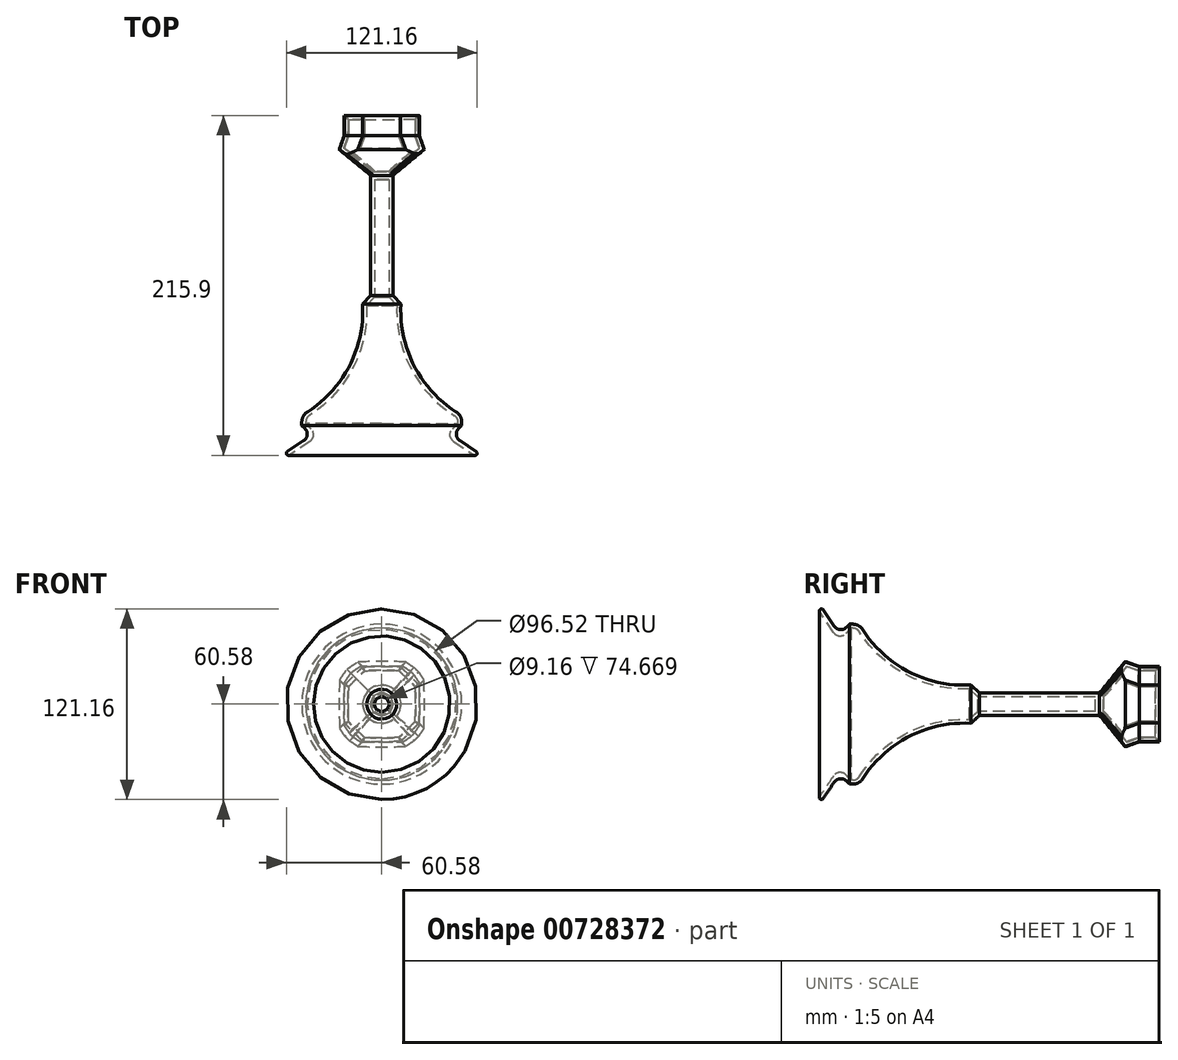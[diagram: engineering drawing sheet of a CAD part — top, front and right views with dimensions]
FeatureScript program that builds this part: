
annotation { "Feature Type Name" : "Feature", "Feature Type Description" : "" }
export const myFeature = defineFeature(function(context is Context, id is Id, definition is map)
    precondition{}
    {
        {
            var Q0;
            Q0=qCreatedBy(makeId("Top.planeOp"),FACE);
            var sketch = newSketch(context, id + "F0", { "sketchPlane" : qUnion([Q0])});
            skLineSegment(sketch, "E0", {"start": v(0, 0) * mm, "end": v(-50.8, 0) * mm});
            skLineSegment(sketch, "E1", {"start": v(0, 0) * mm, "end": v(50.8, 0) * mm});
            skLineSegment(sketch, "E2", {"start": v(-50.8, 0) * mm, "end": v(-50.8, 12.7) * mm});
            skLineSegment(sketch, "E3", {"start": v(50.8, 0) * mm, "end": v(50.8, 12.7) * mm});
            skLineSegment(sketch, "E4", {"start": v(0, 0) * mm, "end": v(0, 88.9) * mm});
            skLineSegment(sketch, "E5", {"start": v(0, 88.9) * mm, "end": v(12.7, 88.9) * mm});
            skLineSegment(sketch, "E6", {"start": v(12.7, 88.9) * mm, "end": v(0, 88.9) * mm});
            skLineSegment(sketch, "E7", {"start": v(0, 88.9) * mm, "end": v(-12.7, 88.9) * mm});
            skArc(sketch, "E8", {"start": v(-50.8, 12.7) * mm, "mid": v(-20.1, 44.98) * mm, "end": v(-12.7, 88.9) * mm});
            skArc(sketch, "E9", {"start": v(12.7, 88.9) * mm, "mid": v(20.1, 44.98) * mm, "end": v(50.8, 12.7) * mm});
            skSolve(sketch);
        }
        {
            var Q0;
            Q0=makeQuery(id+"F0.imprint","IMPRINT",FACE,{"disambiguationData":[TD([[makeQuery(id+"F0.imprint","IMPRINT",EDGE,{"derivedFrom":sQuery(id+"F0.wireOp",EDGE,"E0")}),-1.0]])]});
            var Q1;
            Q1=sQuery(id+"F0.wireOp",EDGE,"E4");
            revolve(context, id + "F1", {"surfaceOperationType" : NewSurfaceOperationType.NEW, "entities" : qUnion([Q0]), "axis" : qUnion([Q1]), "revolveType" : RevolveType.FULL});
        }
        {
            var Q0;
            Q0=makeQuery(id+"F1.opRevolve","SWEPT_EDGE",EDGE,{"disambiguationData":[OSD([sQuery(id+"F0.wireOp",EDGE,"E2"),sQuery(id+"F0.wireOp",EDGE,"E8")])]});
            fillet(context, id + "F2", {"entities" : qUnion([Q0]), "radius" : 7.62 * mm, "tangentPropagation" : true, "allowEdgeOverflow" : false});
        }
        {
            var Q0;
            Q0=makeQuery(id+"F1.opRevolve","SWEPT_EDGE",EDGE,{"disambiguationData":[OSD([sQuery(id+"F0.wireOp",EDGE,"E7"),sQuery(id+"F0.wireOp",EDGE,"E8")])]});
            chamfer(context, id + "F3", {"entities" : qUnion([Q0]), "width" : 5.08 * mm, "tangentPropagation" : true});
        }
        {
            var Q0;
            Q0=makeQuery(id+"F1.opRevolve","SWEPT_EDGE",EDGE,{"disambiguationData":[OSD([sQuery(id+"F0.wireOp",EDGE,"E0"),sQuery(id+"F0.wireOp",EDGE,"E2")])]});
            chamfer(context, id + "F4", {"entities" : qUnion([Q0]), "width" : 6.35 * mm, "tangentPropagation" : true});
        }
        {
            var Q0;
            Q0=makeQuery(id+"F1.opRevolve","SWEPT_FACE",FACE,{"disambiguationData":[OSD([sQuery(id+"F0.wireOp",EDGE,"E7")])]});
            extrude(context, id + "F5", {"entities" : qUnion([Q0]), "operationType" : NewBodyOperationType.ADD, "depth" : 76.2 * mm, "offsetDistance" : 25.4 * mm});
        }
        {
            var Q0;
            Q0=makeQuery(id+"F5.opExtrude","CAP_FACE",FACE,{"disambiguationData":[OSD([sQuery(id+"F0.wireOp",EDGE,"E7")])],"isStart":false});
            cPlane(context, id + "F6", {"entities" : qUnion([Q0]), "cplaneType" : CPlaneType.OFFSET, "offset" : 25.4 * mm, "width" : 152.4 * mm, "height" : 152.4 * mm});
        }
        {
            var Q0;
            Q0=qCreatedBy(id+"F6.planeOp",FACE);
            var sketch = newSketch(context, id + "F7", { "sketchPlane" : qUnion([Q0])});
            skLineSegment(sketch, "E10.bottom", {"start": v(-38.1, 38.1) * mm, "end": v(38.1, 38.1) * mm});
            skLineSegment(sketch, "E10.top", {"start": v(-38.1, -38.1) * mm, "end": v(38.1, -38.1) * mm});
            skLineSegment(sketch, "E10.left", {"start": v(-38.1, 38.1) * mm, "end": v(-38.1, -38.1) * mm});
            skLineSegment(sketch, "E10.right", {"start": v(38.1, 38.1) * mm, "end": v(38.1, -38.1) * mm});
            skPoint(sketch, "E10.middle", {"position": v(0, 0) * mm});
            skSolve(sketch);
        }
        {
            var Q0;
            Q0=makeQuery(id+"F7.imprint","IMPRINT",FACE,{"disambiguationData":[TD([[makeQuery(id+"F7.imprint","IMPRINT",EDGE,{"derivedFrom":sQuery(id+"F7.wireOp",EDGE,"E10.bottom")}),-1.0]])]});
            var Q1;
            Q1=makeQuery(id+"F5.opExtrude","CAP_FACE",FACE,{"disambiguationData":[OSD([sQuery(id+"F0.wireOp",EDGE,"E7")])],"isStart":false});
            loft(context, id + "F8", {"sheetProfilesArray" : [{ "sheetProfileEntities" : qUnion([Q0]) }, { "sheetProfileEntities" : qUnion([Q1]) }]});
        }
        {
            var Q0;
            Q0=makeQuery(id+"F8.opLoft","MID_CAP_EDGE",EDGE,{"disambiguationData":[OSD([sQuery(id+"F7.wireOp",EDGE,"E10.bottom"),sQuery(id+"F7.wireOp",EDGE,"E10.top"),sQuery(id+"F7.wireOp",EDGE,"E10.left")])],"capPos":0.0});
            var Q1;
            Q1=makeQuery(id+"F8.opLoft","MID_CAP_EDGE",EDGE,{"disambiguationData":[OSD([sQuery(id+"F7.wireOp",EDGE,"E10.bottom"),sQuery(id+"F7.wireOp",EDGE,"E10.left"),sQuery(id+"F7.wireOp",EDGE,"E10.right")])],"capPos":0.0});
            var Q2;
            Q2=makeQuery(id+"F8.opLoft","MID_CAP_EDGE",EDGE,{"disambiguationData":[OSD([sQuery(id+"F7.wireOp",EDGE,"E10.bottom"),sQuery(id+"F7.wireOp",EDGE,"E10.top"),sQuery(id+"F7.wireOp",EDGE,"E10.right")])],"capPos":0.0});
            var Q3;
            Q3=makeQuery(id+"F8.opLoft","MID_CAP_EDGE",EDGE,{"disambiguationData":[OSD([sQuery(id+"F7.wireOp",EDGE,"E10.top"),sQuery(id+"F7.wireOp",EDGE,"E10.left"),sQuery(id+"F7.wireOp",EDGE,"E10.right")])],"capPos":0.0});
            chamfer(context, id + "F9", {"entities" : qUnion([Q0, Q1, Q2, Q3]), "width" : 5.08 * mm, "tangentPropagation" : true});
        }
        {
            var Q0;
            Q0=makeQuery(id+"F8.opLoft","SWEPT_EDGE",EDGE,{"disambiguationData":[OSD([sQuery(id+"F0.wireOp",EDGE,"E7"),sQuery(id+"F0.wireOp",EDGE,"E8"),sQuery(id+"F7.wireOp",EDGE,"E10.bottom"),sQuery(id+"F7.wireOp",EDGE,"E10.left"),sQuery(id+"F7.wireOp",EDGE,"E10.right")])]});
            var Q1;
            Q1=makeQuery(id+"F8.opLoft","SWEPT_EDGE",EDGE,{"disambiguationData":[OSD([sQuery(id+"F0.wireOp",EDGE,"E7"),sQuery(id+"F0.wireOp",EDGE,"E8"),sQuery(id+"F7.wireOp",EDGE,"E10.bottom"),sQuery(id+"F7.wireOp",EDGE,"E10.top"),sQuery(id+"F7.wireOp",EDGE,"E10.right")])]});
            var Q2;
            Q2=makeQuery(id+"F8.opLoft","SWEPT_EDGE",EDGE,{"disambiguationData":[OSD([sQuery(id+"F0.wireOp",EDGE,"E7"),sQuery(id+"F0.wireOp",EDGE,"E8"),sQuery(id+"F7.wireOp",EDGE,"E10.top"),sQuery(id+"F7.wireOp",EDGE,"E10.left"),sQuery(id+"F7.wireOp",EDGE,"E10.right")])]});
            var Q3;
            Q3=makeQuery(id+"F8.opLoft","SWEPT_EDGE",EDGE,{"disambiguationData":[OSD([sQuery(id+"F7.wireOp",EDGE,"E10.bottom"),sQuery(id+"F7.wireOp",EDGE,"E10.left")])]});
            chamfer(context, id + "F10", {"entities" : qUnion([Q0, Q1, Q2, Q3]), "width" : 5.08 * mm, "tangentPropagation" : true});
        }
        {
            var Q0;
            Q0=makeQuery(id+"F1.opRevolve","SWEPT_FACE",FACE,{"disambiguationData":[OSD([sQuery(id+"F0.wireOp",EDGE,"E0")])]});
            cPlane(context, id + "F11", {"entities" : qUnion([Q0]), "cplaneType" : CPlaneType.OFFSET, "offset" : 12.7 * mm, "width" : 152.4 * mm, "height" : 152.4 * mm});
        }
        {
            var Q0;
            Q0=qCreatedBy(id+"F11.planeOp",FACE);
            var sketch = newSketch(context, id + "F12", { "sketchPlane" : qUnion([Q0])});
            skCircle(sketch, "E11", {"center": v(0, 0) * mm, "radius": 63.5 * mm});
            skSolve(sketch);
        }
        {
            var Q1;
            Q1=makeQuery(id+"F1.opRevolve","SWEPT_FACE",FACE,{"disambiguationData":[OSD([sQuery(id+"F0.wireOp",EDGE,"E0")])]});
            var Q2;
            Q2=makeQuery(id+"F12.imprint","IMPRINT",FACE,{"disambiguationData":[TD([[makeQuery(id+"F12.imprint","IMPRINT",EDGE,{"derivedFrom":sQuery(id+"F12.wireOp",EDGE,"E11")}),1.0]])]});
            loft(context, id + "F13", {"operationType" : NewBodyOperationType.ADD, "sheetProfilesArray" : [{ "sheetProfileEntities" : qUnion([Q1]) }, { "sheetProfileEntities" : qUnion([Q2]) }]});
        }
        {
            var Q0;
            Q0=makeQuery(id+"F13.opLoft","CAP_FACE",FACE,{"disambiguationData":[OSD([makeQuery(id+"F12.imprint","IMPRINT",FACE,{"disambiguationData":[TD([[makeQuery(id+"F12.imprint","IMPRINT",EDGE,{"derivedFrom":sQuery(id+"F12.wireOp",EDGE,"E11")}),1.0]])]})])],"isStart":true});
            shell(context, id + "F14", {"entities" : qUnion([Q0]), "thickness" : 2.54 * mm});
        }
        {
            var Q0;
            Q0=makeQuery(id+"F13.opLoft","CAP_FACE",FACE,{"disambiguationData":[OSD([makeQuery(id+"F12.imprint","IMPRINT",FACE,{"disambiguationData":[TD([[makeQuery(id+"F12.imprint","IMPRINT",EDGE,{"derivedFrom":sQuery(id+"F12.wireOp",EDGE,"E11")}),1.0]])]})])],"isStart":true});
            fillet(context, id + "F15", {"entities" : qUnion([Q0]), "radius" : 1.27 * mm, "tangentPropagation" : true, "allowEdgeOverflow" : false});
        }
        {
            var Q0;
            {var subQ0=sQuery(id+"F0.wireOp",EDGE,"E2");var subQ1=sQuery(id+"F0.wireOp",EDGE,"E0");Q0=makeQuery(id+"F13.boolean.opBoolean","MERGE",EDGE,{"derivedFrom":[makeQuery(id+"F4.opChamfer","BLEND_EDGE",EDGE,{"blendedFrom":[makeQuery(id+"F1.opRevolve","SWEPT_EDGE",EDGE,{"disambiguationData":[OSD([subQ1,subQ0])]}),makeQuery(id+"F1.opRevolve","SWEPT_FACE",FACE,{"disambiguationData":[OSD([subQ1])]})],"blendedInto":[makeQuery(id+"F1.opRevolve","SWEPT_FACE",FACE,{"disambiguationData":[OSD([subQ1])]})]}),makeQuery(id+"F13.opLoft","MID_CAP_EDGE",EDGE,{"disambiguationData":[OSD([subQ1,subQ0])],"capPos":0.0})]});}
            fillet(context, id + "F16", {"entities" : qUnion([Q0]), "radius" : 5.08 * mm, "tangentPropagation" : true, "allowEdgeOverflow" : false});
        }
        {
            var Q0;
            {var subQ0=sQuery(id+"F0.wireOp",EDGE,"E2");var subQ1=sQuery(id+"F0.wireOp",EDGE,"E0");Q0=makeQuery(id+"F14.opShell","OFFSET_EDGE",EDGE,{"disambiguationData":[OSD([subQ1,subQ0]),TDD([makeQuery(id+"F13.boolean.opBoolean","MERGE",EDGE,{"derivedFrom":[makeQuery(id+"F4.opChamfer","BLEND_EDGE",EDGE,{"blendedFrom":[makeQuery(id+"F1.opRevolve","SWEPT_EDGE",EDGE,{"disambiguationData":[OSD([subQ1,subQ0])]}),makeQuery(id+"F1.opRevolve","SWEPT_FACE",FACE,{"disambiguationData":[OSD([subQ1])]})],"blendedInto":[makeQuery(id+"F1.opRevolve","SWEPT_FACE",FACE,{"disambiguationData":[OSD([subQ1])]})]}),makeQuery(id+"F13.opLoft","MID_CAP_EDGE",EDGE,{"disambiguationData":[OSD([subQ1,subQ0])],"capPos":0.0})]})])]});}
            fillet(context, id + "F17", {"entities" : qUnion([Q0]), "radius" : 5.08 * mm, "tangentPropagation" : true, "allowEdgeOverflow" : false});
        }
        {
            var Q0;
            {var subQ0=sQuery(id+"F7.wireOp",EDGE,"E10.left");var subQ1=sQuery(id+"F7.wireOp",EDGE,"E10.top");Q0=makeQuery(id+"F9.opChamfer","BLEND_EDGE",EDGE,{"blendedFrom":[makeQuery(id+"F8.opLoft","MID_CAP_EDGE",EDGE,{"disambiguationData":[OSD([sQuery(id+"F7.wireOp",EDGE,"E10.bottom"),subQ1,subQ0])],"capPos":0.0}),makeQuery(id+"F8.opLoft","MID_CAP_EDGE",EDGE,{"disambiguationData":[OSD([subQ1,subQ0,sQuery(id+"F7.wireOp",EDGE,"E10.right")])],"capPos":0.0})],"blendedInto":[]});}
            var Q1;
            {var subQ0=sQuery(id+"F7.wireOp",EDGE,"E10.left");var subQ1=sQuery(id+"F7.wireOp",EDGE,"E10.bottom");Q1=makeQuery(id+"F9.opChamfer","BLEND_EDGE",EDGE,{"blendedFrom":[makeQuery(id+"F8.opLoft","MID_CAP_EDGE",EDGE,{"disambiguationData":[OSD([subQ1,subQ0,sQuery(id+"F7.wireOp",EDGE,"E10.right")])],"capPos":0.0}),makeQuery(id+"F8.opLoft","MID_CAP_EDGE",EDGE,{"disambiguationData":[OSD([subQ1,sQuery(id+"F7.wireOp",EDGE,"E10.top"),subQ0])],"capPos":0.0})],"blendedInto":[]});}
            var Q2;
            {var subQ0=sQuery(id+"F7.wireOp",EDGE,"E10.right");var subQ1=sQuery(id+"F7.wireOp",EDGE,"E10.top");Q2=makeQuery(id+"F9.opChamfer","BLEND_EDGE",EDGE,{"blendedFrom":[makeQuery(id+"F8.opLoft","MID_CAP_EDGE",EDGE,{"disambiguationData":[OSD([sQuery(id+"F7.wireOp",EDGE,"E10.bottom"),subQ1,subQ0])],"capPos":0.0}),makeQuery(id+"F8.opLoft","MID_CAP_EDGE",EDGE,{"disambiguationData":[OSD([subQ1,sQuery(id+"F7.wireOp",EDGE,"E10.left"),subQ0])],"capPos":0.0})],"blendedInto":[]});}
            var Q3;
            {var subQ0=sQuery(id+"F7.wireOp",EDGE,"E10.right");var subQ1=sQuery(id+"F7.wireOp",EDGE,"E10.bottom");Q3=makeQuery(id+"F9.opChamfer","BLEND_EDGE",EDGE,{"blendedFrom":[makeQuery(id+"F8.opLoft","MID_CAP_EDGE",EDGE,{"disambiguationData":[OSD([subQ1,sQuery(id+"F7.wireOp",EDGE,"E10.left"),subQ0])],"capPos":0.0}),makeQuery(id+"F8.opLoft","MID_CAP_EDGE",EDGE,{"disambiguationData":[OSD([subQ1,sQuery(id+"F7.wireOp",EDGE,"E10.top"),subQ0])],"capPos":0.0})],"blendedInto":[]});}
            chamfer(context, id + "F18", {"entities" : qUnion([Q0, Q1, Q2, Q3]), "width" : 12.7 * mm, "tangentPropagation" : true});
        }
        {
            var Q0;
            Q0=makeQuery(id+"F8.opLoft","CAP_FACE",FACE,{"disambiguationData":[OSD([makeQuery(id+"F7.imprint","IMPRINT",FACE,{"disambiguationData":[TD([[makeQuery(id+"F7.imprint","IMPRINT",EDGE,{"derivedFrom":sQuery(id+"F7.wireOp",EDGE,"E10.bottom")}),-1.0]])]})])],"isStart":true});
            extrude(context, id + "F19", {"entities" : qUnion([Q0]), "operationType" : NewBodyOperationType.ADD, "depth" : 2.54 * mm, "offsetDistance" : 25.4 * mm});
        }
        {
            var Q0;
            Q0=makeQuery(id+"F19.opExtrude","CAP_FACE",FACE,{"disambiguationData":[OSD([makeQuery(id+"F7.imprint","IMPRINT",FACE,{"disambiguationData":[TD([[makeQuery(id+"F7.imprint","IMPRINT",EDGE,{"derivedFrom":sQuery(id+"F7.wireOp",EDGE,"E10.bottom")}),-1.0]])]})])],"isStart":false});
            extrude(context, id + "F20", {"entities" : qUnion([Q0]), "operationType" : NewBodyOperationType.ADD, "depth" : 12.7 * mm, "offsetDistance" : 25.4 * mm});
        }
        {
            var Q0;
            Q0=makeQuery(id+"F20.opExtrude","CAP_FACE",FACE,{"disambiguationData":[OSD([makeQuery(id+"F7.imprint","IMPRINT",FACE,{"disambiguationData":[TD([[makeQuery(id+"F7.imprint","IMPRINT",EDGE,{"derivedFrom":sQuery(id+"F7.wireOp",EDGE,"E10.bottom")}),-1.0]])]})])],"isStart":false});
            shell(context, id + "F21", {"entities" : qUnion([Q0]), "thickness" : 2.54 * mm});
        }
        {
            var Q0;
            {var subQ0=sQuery(id+"F7.wireOp",EDGE,"E10.bottom");var subQ1=sQuery(id+"F7.wireOp",EDGE,"E10.left");var subQ2=sQuery(id+"F7.wireOp",EDGE,"E10.right");var subQ3=makeQuery(id+"F7.imprint","IMPRINT",FACE,{"disambiguationData":[TD([[makeQuery(id+"F7.imprint","IMPRINT",EDGE,{"derivedFrom":subQ0}),-1.0]])]});Q0=makeQuery(id+"F21.opShell","OFFSET_EDGE",EDGE,{"disambiguationData":[OSD([subQ0,subQ1,subQ2,subQ3]),TDD([makeQuery(id+"F20.opExtrude","CAP_EDGE",EDGE,{"disambiguationData":[OSD([subQ0,subQ1,subQ2,subQ3])],"isStart":false})])]});}
            var Q1;
            {var subQ0=sQuery(id+"F7.wireOp",EDGE,"E10.bottom");var subQ1=sQuery(id+"F7.wireOp",EDGE,"E10.top");var subQ2=sQuery(id+"F7.wireOp",EDGE,"E10.left");var subQ3=sQuery(id+"F7.wireOp",EDGE,"E10.right");var subQ4=makeQuery(id+"F7.imprint","IMPRINT",FACE,{"disambiguationData":[TD([[makeQuery(id+"F7.imprint","IMPRINT",EDGE,{"derivedFrom":subQ0}),-1.0]])]});Q1=makeQuery(id+"F21.opShell","OFFSET_EDGE",EDGE,{"disambiguationData":[OSD([subQ0,subQ1,subQ2,subQ3,subQ4]),TDD([makeQuery(id+"F20.opExtrude","CAP_EDGE",EDGE,{"disambiguationData":[OSD([subQ0,subQ1,subQ2,subQ3,subQ4]),TDD([makeQuery(id+"F19.opExtrude","CAP_EDGE",EDGE,{"disambiguationData":[OSD([subQ0,subQ1,subQ2,subQ3,subQ4]),TDD([makeQuery(id+"F18.opChamfer","BLEND_EDGE",EDGE,{"blendedFrom":[makeQuery(id+"F9.opChamfer","BLEND_EDGE",EDGE,{"blendedFrom":[makeQuery(id+"F8.opLoft","MID_CAP_EDGE",EDGE,{"disambiguationData":[OSD([subQ0,subQ2,subQ3])],"capPos":0.0}),makeQuery(id+"F8.opLoft","MID_CAP_EDGE",EDGE,{"disambiguationData":[OSD([subQ0,subQ1,subQ3])],"capPos":0.0})],"blendedInto":[]}),makeQuery(id+"F8.opLoft","CAP_FACE",FACE,{"disambiguationData":[OSD([subQ4])],"isStart":true})],"blendedInto":[makeQuery(id+"F8.opLoft","CAP_FACE",FACE,{"disambiguationData":[OSD([subQ4])],"isStart":true})]})])],"isStart":false})])],"isStart":false})])]});}
            var Q2;
            {var subQ0=sQuery(id+"F7.wireOp",EDGE,"E10.bottom");var subQ1=sQuery(id+"F7.wireOp",EDGE,"E10.top");var subQ2=sQuery(id+"F7.wireOp",EDGE,"E10.right");var subQ3=makeQuery(id+"F7.imprint","IMPRINT",FACE,{"disambiguationData":[TD([[makeQuery(id+"F7.imprint","IMPRINT",EDGE,{"derivedFrom":subQ0}),-1.0]])]});Q2=makeQuery(id+"F21.opShell","OFFSET_EDGE",EDGE,{"disambiguationData":[OSD([subQ0,subQ1,subQ2,subQ3]),TDD([makeQuery(id+"F20.opExtrude","CAP_EDGE",EDGE,{"disambiguationData":[OSD([subQ0,subQ1,subQ2,subQ3])],"isStart":false})])]});}
            var Q3;
            {var subQ0=sQuery(id+"F7.wireOp",EDGE,"E10.bottom");var subQ1=sQuery(id+"F7.wireOp",EDGE,"E10.top");var subQ2=sQuery(id+"F7.wireOp",EDGE,"E10.left");var subQ3=sQuery(id+"F7.wireOp",EDGE,"E10.right");var subQ4=makeQuery(id+"F7.imprint","IMPRINT",FACE,{"disambiguationData":[TD([[makeQuery(id+"F7.imprint","IMPRINT",EDGE,{"derivedFrom":subQ0}),-1.0]])]});Q3=makeQuery(id+"F21.opShell","OFFSET_EDGE",EDGE,{"disambiguationData":[OSD([subQ0,subQ1,subQ2,subQ3,subQ4]),TDD([makeQuery(id+"F20.opExtrude","CAP_EDGE",EDGE,{"disambiguationData":[OSD([subQ0,subQ1,subQ2,subQ3,subQ4]),TDD([makeQuery(id+"F19.opExtrude","CAP_EDGE",EDGE,{"disambiguationData":[OSD([subQ0,subQ1,subQ2,subQ3,subQ4]),TDD([makeQuery(id+"F18.opChamfer","BLEND_EDGE",EDGE,{"blendedFrom":[makeQuery(id+"F9.opChamfer","BLEND_EDGE",EDGE,{"blendedFrom":[makeQuery(id+"F8.opLoft","MID_CAP_EDGE",EDGE,{"disambiguationData":[OSD([subQ0,subQ2,subQ3])],"capPos":0.0}),makeQuery(id+"F8.opLoft","MID_CAP_EDGE",EDGE,{"disambiguationData":[OSD([subQ0,subQ1,subQ2])],"capPos":0.0})],"blendedInto":[]}),makeQuery(id+"F8.opLoft","CAP_FACE",FACE,{"disambiguationData":[OSD([subQ4])],"isStart":true})],"blendedInto":[makeQuery(id+"F8.opLoft","CAP_FACE",FACE,{"disambiguationData":[OSD([subQ4])],"isStart":true})]})])],"isStart":false})])],"isStart":false})])]});}
            var Q4;
            {var subQ0=sQuery(id+"F7.wireOp",EDGE,"E10.bottom");var subQ1=sQuery(id+"F7.wireOp",EDGE,"E10.top");var subQ2=sQuery(id+"F7.wireOp",EDGE,"E10.left");var subQ3=makeQuery(id+"F7.imprint","IMPRINT",FACE,{"disambiguationData":[TD([[makeQuery(id+"F7.imprint","IMPRINT",EDGE,{"derivedFrom":subQ0}),-1.0]])]});Q4=makeQuery(id+"F21.opShell","OFFSET_EDGE",EDGE,{"disambiguationData":[OSD([subQ0,subQ1,subQ2,subQ3]),TDD([makeQuery(id+"F20.opExtrude","CAP_EDGE",EDGE,{"disambiguationData":[OSD([subQ0,subQ1,subQ2,subQ3])],"isStart":false})])]});}
            var Q5;
            {var subQ0=sQuery(id+"F7.wireOp",EDGE,"E10.bottom");var subQ1=sQuery(id+"F7.wireOp",EDGE,"E10.top");var subQ2=sQuery(id+"F7.wireOp",EDGE,"E10.left");var subQ3=sQuery(id+"F7.wireOp",EDGE,"E10.right");var subQ4=makeQuery(id+"F7.imprint","IMPRINT",FACE,{"disambiguationData":[TD([[makeQuery(id+"F7.imprint","IMPRINT",EDGE,{"derivedFrom":subQ0}),-1.0]])]});Q5=makeQuery(id+"F21.opShell","OFFSET_EDGE",EDGE,{"disambiguationData":[OSD([subQ0,subQ1,subQ2,subQ3,subQ4]),TDD([makeQuery(id+"F20.opExtrude","CAP_EDGE",EDGE,{"disambiguationData":[OSD([subQ0,subQ1,subQ2,subQ3,subQ4]),TDD([makeQuery(id+"F19.opExtrude","CAP_EDGE",EDGE,{"disambiguationData":[OSD([subQ0,subQ1,subQ2,subQ3,subQ4]),TDD([makeQuery(id+"F18.opChamfer","BLEND_EDGE",EDGE,{"blendedFrom":[makeQuery(id+"F9.opChamfer","BLEND_EDGE",EDGE,{"blendedFrom":[makeQuery(id+"F8.opLoft","MID_CAP_EDGE",EDGE,{"disambiguationData":[OSD([subQ0,subQ1,subQ2])],"capPos":0.0}),makeQuery(id+"F8.opLoft","MID_CAP_EDGE",EDGE,{"disambiguationData":[OSD([subQ1,subQ2,subQ3])],"capPos":0.0})],"blendedInto":[]}),makeQuery(id+"F8.opLoft","CAP_FACE",FACE,{"disambiguationData":[OSD([subQ4])],"isStart":true})],"blendedInto":[makeQuery(id+"F8.opLoft","CAP_FACE",FACE,{"disambiguationData":[OSD([subQ4])],"isStart":true})]})])],"isStart":false})])],"isStart":false})])]});}
            var Q6;
            {var subQ0=sQuery(id+"F7.wireOp",EDGE,"E10.bottom");var subQ1=sQuery(id+"F7.wireOp",EDGE,"E10.top");var subQ2=sQuery(id+"F7.wireOp",EDGE,"E10.left");var subQ3=sQuery(id+"F7.wireOp",EDGE,"E10.right");var subQ4=makeQuery(id+"F7.imprint","IMPRINT",FACE,{"disambiguationData":[TD([[makeQuery(id+"F7.imprint","IMPRINT",EDGE,{"derivedFrom":subQ0}),-1.0]])]});Q6=makeQuery(id+"F21.opShell","OFFSET_EDGE",EDGE,{"disambiguationData":[OSD([subQ0,subQ1,subQ2,subQ3,subQ4]),TDD([makeQuery(id+"F20.opExtrude","CAP_EDGE",EDGE,{"disambiguationData":[OSD([subQ0,subQ1,subQ2,subQ3,subQ4]),TDD([makeQuery(id+"F19.opExtrude","CAP_EDGE",EDGE,{"disambiguationData":[OSD([subQ0,subQ1,subQ2,subQ3,subQ4]),TDD([makeQuery(id+"F18.opChamfer","BLEND_EDGE",EDGE,{"blendedFrom":[makeQuery(id+"F9.opChamfer","BLEND_EDGE",EDGE,{"blendedFrom":[makeQuery(id+"F8.opLoft","MID_CAP_EDGE",EDGE,{"disambiguationData":[OSD([subQ0,subQ1,subQ3])],"capPos":0.0}),makeQuery(id+"F8.opLoft","MID_CAP_EDGE",EDGE,{"disambiguationData":[OSD([subQ1,subQ2,subQ3])],"capPos":0.0})],"blendedInto":[]}),makeQuery(id+"F8.opLoft","CAP_FACE",FACE,{"disambiguationData":[OSD([subQ4])],"isStart":true})],"blendedInto":[makeQuery(id+"F8.opLoft","CAP_FACE",FACE,{"disambiguationData":[OSD([subQ4])],"isStart":true})]})])],"isStart":false})])],"isStart":false})])]});}
            var Q7;
            {var subQ0=sQuery(id+"F7.wireOp",EDGE,"E10.top");var subQ1=sQuery(id+"F7.wireOp",EDGE,"E10.left");var subQ2=sQuery(id+"F7.wireOp",EDGE,"E10.right");var subQ3=makeQuery(id+"F7.imprint","IMPRINT",FACE,{"disambiguationData":[TD([[makeQuery(id+"F7.imprint","IMPRINT",EDGE,{"derivedFrom":sQuery(id+"F7.wireOp",EDGE,"E10.bottom")}),-1.0]])]});Q7=makeQuery(id+"F21.opShell","OFFSET_EDGE",EDGE,{"disambiguationData":[OSD([subQ0,subQ1,subQ2,subQ3]),TDD([makeQuery(id+"F20.opExtrude","CAP_EDGE",EDGE,{"disambiguationData":[OSD([subQ0,subQ1,subQ2,subQ3])],"isStart":false})])]});}
            chamfer(context, id + "F22", {"entities" : qUnion([Q0, Q1, Q2, Q3, Q4, Q5, Q6, Q7]), "width" : 5.08 * mm, "tangentPropagation" : true});
        }
    });
